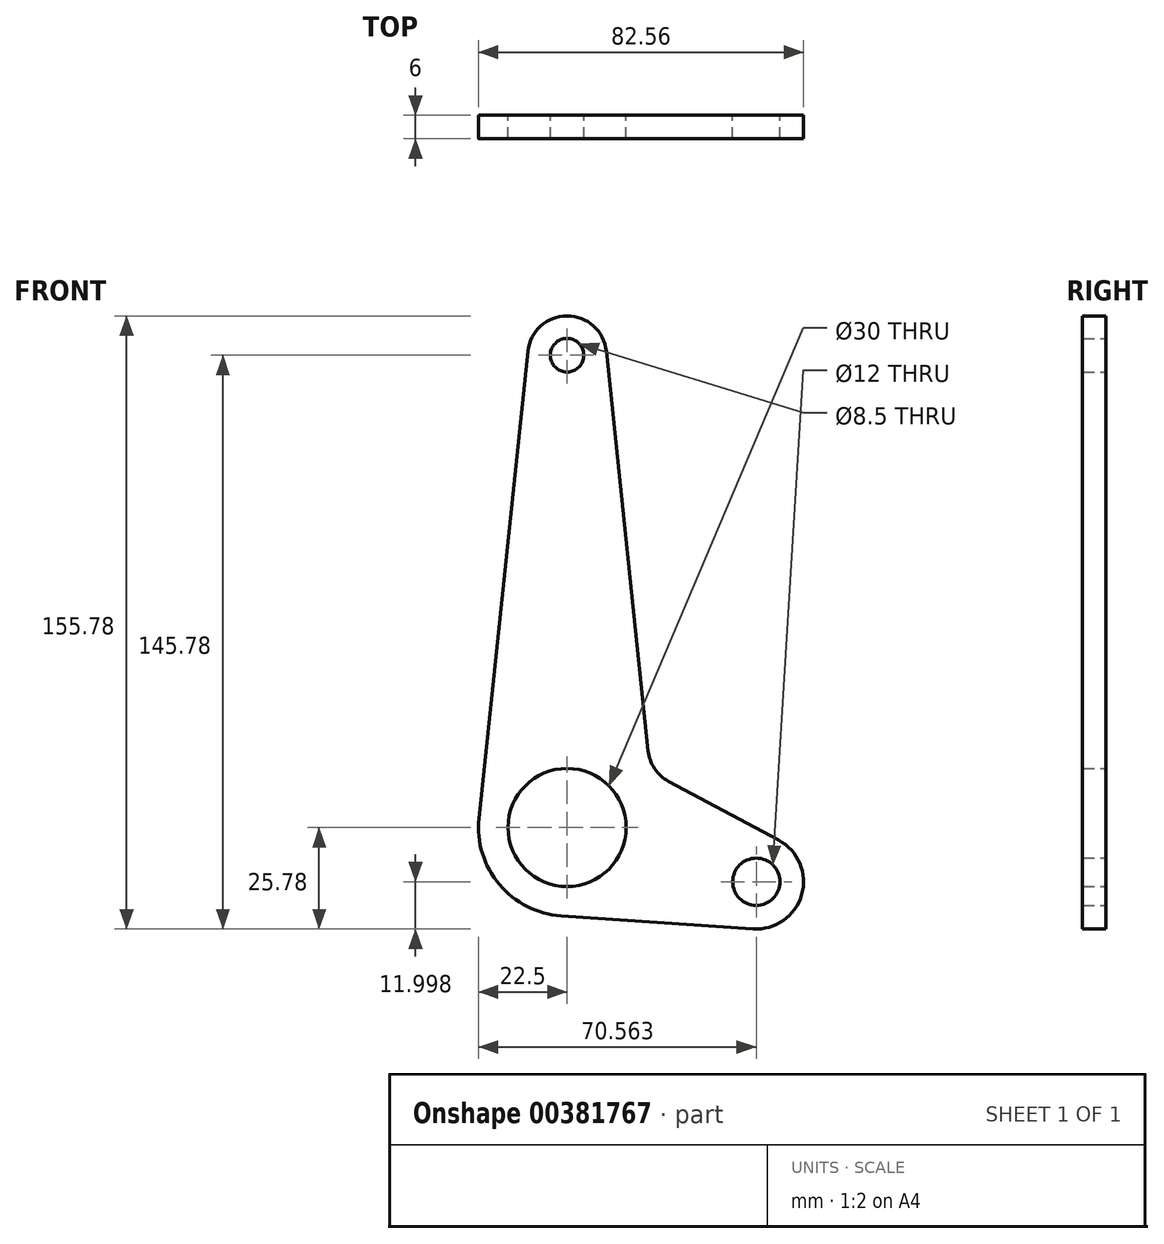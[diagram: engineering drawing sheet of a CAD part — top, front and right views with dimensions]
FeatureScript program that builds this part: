
annotation { "Feature Type Name" : "Feature", "Feature Type Description" : "" }
export const myFeature = defineFeature(function(context is Context, id is Id, definition is map)
    precondition{}
    {
        {
            var Q0;
            Q0=qCreatedBy(makeId("Front.planeOp"),FACE);
            var sketch = newSketch(context, id + "F0", { "sketchPlane" : qUnion([Q0])});
            skCircle(sketch, "E0", {"center": v(0, 0) * mm, "radius": 15 * mm});
            skCircle(sketch, "E1", {"center": v(48.06, -13.78) * mm, "radius": 6 * mm});
            skCircle(sketch, "E2", {"center": v(0, 120) * mm, "radius": 4.25 * mm});
            skLineSegment(sketch, "E3", {"start": v(0, 120) * mm, "end": v(0, 0) * mm, "construction": true});
            skLineSegment(sketch, "E4", {"start": v(0, 0) * mm, "end": v(48.06, -13.78) * mm, "construction": true});
            skArc(sketch, "E5", {"start": v(-22.38, 2.34) * mm, "mid": v(-17.22, -14.48) * mm, "end": v(-1.52, -22.45) * mm});
            skLineSegment(sketch, "E6", {"start": v(-9.95, 121.04) * mm, "end": v(-22.38, 2.34) * mm});
            skArc(sketch, "E7", {"start": v(53.72, -3.2) * mm, "mid": v(59.6, -17.1) * mm, "end": v(47.25, -25.75) * mm});
            skLineSegment(sketch, "E8", {"start": v(53.72, -3.2) * mm, "end": v(25.81, 11.72) * mm});
            skLineSegment(sketch, "E9", {"start": v(-1.52, -22.45) * mm, "end": v(47.25, -25.75) * mm});
            skPoint(sketch, "E10.trimOffspring.end.orphan", {"position": v(22.38, 2.34) * mm});
            skLineSegment(sketch, "E11", {"start": v(9.95, 121.04) * mm, "end": v(20.58, 19.5) * mm});
            skPoint(sketch, "E12.center.orphan", {"position": v(30.53, 20.54) * mm});
            skArc(sketch, "E13", {"start": v(25.81, 11.72) * mm, "mid": v(22.23, 14.96) * mm, "end": v(20.58, 19.5) * mm});
            skArc(sketch, "E14", {"start": v(-9.95, 121.04) * mm, "mid": v(0, 130) * mm, "end": v(9.95, 121.04) * mm});
            skSolve(sketch);
        }
        {
            var Q0;
            Q0=makeQuery(id+"F0.imprint","IMPRINT",FACE,{"disambiguationData":[TD([[makeQuery(id+"F0.imprint","IMPRINT",EDGE,{"derivedFrom":sQuery(id+"F0.wireOp",EDGE,"E0")}),-1.0]])]});
            extrude(context, id + "F1", {"entities" : qUnion([Q0]), "depth" : 6 * mm});
        }
    });
